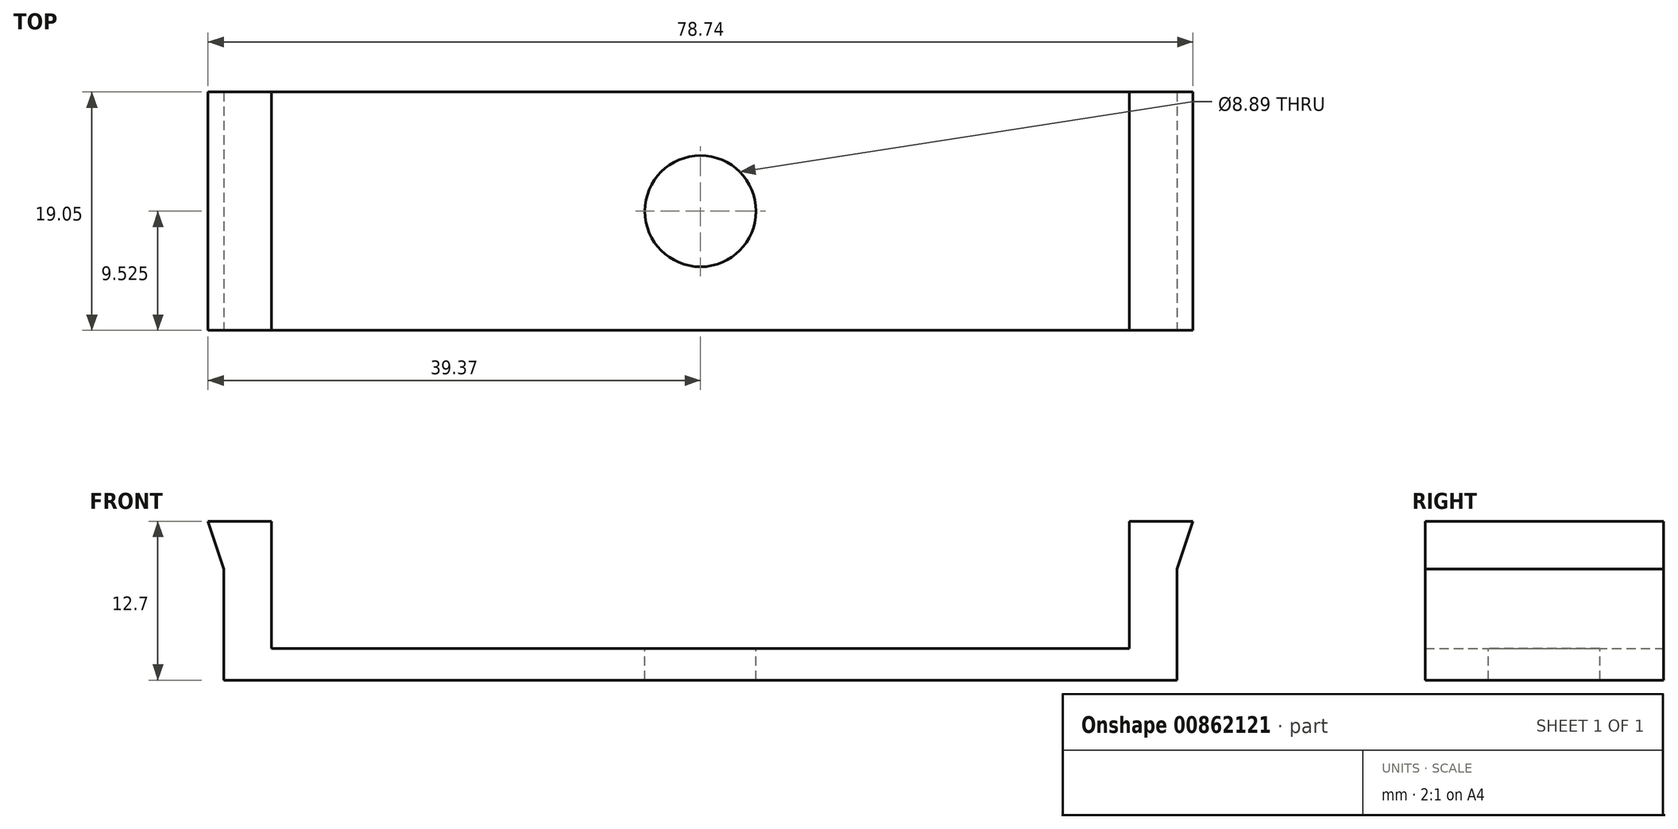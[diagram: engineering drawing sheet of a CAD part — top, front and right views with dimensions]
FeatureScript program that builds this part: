
annotation { "Feature Type Name" : "Feature", "Feature Type Description" : "" }
export const myFeature = defineFeature(function(context is Context, id is Id, definition is map)
    precondition{}
    {
        {
            var Q0;
            Q0=qCreatedBy(makeId("Top.planeOp"),FACE);
            var sketch = newSketch(context, id + "F0", { "sketchPlane" : qUnion([Q0])});
            skLineSegment(sketch, "E0.bottom", {"start": v(0, 0) * mm, "end": v(76.2, 0) * mm});
            skLineSegment(sketch, "E0.top", {"start": v(0, 19.05) * mm, "end": v(76.2, 19.05) * mm});
            skLineSegment(sketch, "E0.left", {"start": v(0, 0) * mm, "end": v(0, 19.05) * mm});
            skLineSegment(sketch, "E0.right", {"start": v(76.2, 0) * mm, "end": v(76.2, 19.05) * mm});
            skSolve(sketch);
        }
        {
            var Q0;
            Q0=makeQuery(id+"F0.imprint","IMPRINT",FACE,{"disambiguationData":[TD([[makeQuery(id+"F0.imprint","IMPRINT",EDGE,{"derivedFrom":sQuery(id+"F0.wireOp",EDGE,"E0.bottom")}),1.0]])]});
            extrude(context, id + "F1", {"entities" : qUnion([Q0]), "depth" : 2.54 * mm, "offsetDistance" : 25.4 * mm});
        }
        {
            var Q0;
            Q0=makeQuery(id+"F1.opExtrude","CAP_FACE",FACE,{"disambiguationData":[OSD([sQuery(id+"F0.wireOp",EDGE,"E0.bottom"),sQuery(id+"F0.wireOp",EDGE,"E0.top"),sQuery(id+"F0.wireOp",EDGE,"E0.left"),sQuery(id+"F0.wireOp",EDGE,"E0.right")])],"isStart":false});
            var sketch = newSketch(context, id + "F2", { "sketchPlane" : qUnion([Q0])});
            skLineSegment(sketch, "E1.bottom", {"start": v(76.2, 19.05) * mm, "end": v(72.4, 19.05) * mm});
            skLineSegment(sketch, "E1.top", {"start": v(76.2, 0) * mm, "end": v(72.4, 0) * mm});
            skLineSegment(sketch, "E1.left", {"start": v(76.2, 19.05) * mm, "end": v(76.2, 0) * mm});
            skLineSegment(sketch, "E1.right", {"start": v(72.4, 19.05) * mm, "end": v(72.4, 0) * mm});
            skLineSegment(sketch, "E2.bottom", {"start": v(0, 0) * mm, "end": v(3.8, 0) * mm});
            skLineSegment(sketch, "E2.top", {"start": v(0, 19.05) * mm, "end": v(3.8, 19.05) * mm});
            skLineSegment(sketch, "E2.left", {"start": v(0, 0) * mm, "end": v(0, 19.05) * mm});
            skLineSegment(sketch, "E2.right", {"start": v(3.8, 0) * mm, "end": v(3.8, 19.05) * mm});
            skSolve(sketch);
        }
        {
            var Q0;
            Q0=makeQuery(id+"F2.imprint","IMPRINT",FACE,{"disambiguationData":[TD([[makeQuery(id+"F2.imprint","IMPRINT",EDGE,{"derivedFrom":sQuery(id+"F2.wireOp",EDGE,"E2.bottom")}),1.0]])]});
            var Q1;
            Q1=makeQuery(id+"F2.imprint","IMPRINT",FACE,{"disambiguationData":[TD([[makeQuery(id+"F2.imprint","IMPRINT",EDGE,{"derivedFrom":sQuery(id+"F2.wireOp",EDGE,"E1.bottom")}),-1.0]])]});
            extrude(context, id + "F3", {"entities" : qUnion([Q0, Q1]), "operationType" : NewBodyOperationType.ADD, "depth" : 10.16 * mm, "offsetDistance" : 25.4 * mm});
        }
        {
            var Q0;
            Q0=makeQuery(id+"F1.opExtrude","CAP_FACE",FACE,{"disambiguationData":[OSD([sQuery(id+"F0.wireOp",EDGE,"E0.bottom"),sQuery(id+"F0.wireOp",EDGE,"E0.top"),sQuery(id+"F0.wireOp",EDGE,"E0.left"),sQuery(id+"F0.wireOp",EDGE,"E0.right")])],"isStart":false});
            var sketch = newSketch(context, id + "F4", { "sketchPlane" : qUnion([Q0])});
            skLineSegment(sketch, "E3", {"start": v(3.81, 9.52) * mm, "end": v(72.4, 9.52) * mm, "construction": true});
            skCircle(sketch, "E4", {"center": v(38.1, 9.52) * mm, "radius": 4.45 * mm});
            skSolve(sketch);
        }
        {
            var Q0;
            Q0=makeQuery(id+"F4.imprint","IMPRINT",FACE,{"disambiguationData":[TD([[makeQuery(id+"F4.imprint","IMPRINT",EDGE,{"derivedFrom":sQuery(id+"F4.wireOp",EDGE,"E4")}),1.0]])]});
            extrude(context, id + "F5", {"entities" : qUnion([Q0]), "operationType" : NewBodyOperationType.REMOVE, "oppositeDirection" : true, "depth" : 25.4 * mm, "offsetDistance" : 25.4 * mm});
        }
        {
            var Q0;
            Q0=makeQuery(id+"F3.boolean.opBoolean","MERGE",FACE,{"derivedFrom":[makeQuery(id+"F1.opExtrude","SWEPT_FACE",FACE,{"disambiguationData":[OSD([sQuery(id+"F0.wireOp",EDGE,"E0.bottom")])]}),makeQuery(id+"F3.opExtrude","SWEPT_FACE",FACE,{"disambiguationData":[OSD([sQuery(id+"F2.wireOp",EDGE,"E1.top")])]}),makeQuery(id+"F3.opExtrude","SWEPT_FACE",FACE,{"disambiguationData":[OSD([sQuery(id+"F2.wireOp",EDGE,"E2.bottom")])]})]});
            var sketch = newSketch(context, id + "F6", { "sketchPlane" : qUnion([Q0])});
            skLineSegment(sketch, "E5", {"start": v(0, 12.7) * mm, "end": v(-1.27, 12.7) * mm});
            skLineSegment(sketch, "E6", {"start": v(-1.27, 12.7) * mm, "end": v(0, 8.9) * mm});
            skLineSegment(sketch, "E7", {"start": v(0, 12.7) * mm, "end": v(0, 8.9) * mm});
            skLineSegment(sketch, "E8", {"start": v(76.2, 12.7) * mm, "end": v(77.47, 12.7) * mm});
            skLineSegment(sketch, "E9", {"start": v(77.47, 12.7) * mm, "end": v(76.2, 8.9) * mm});
            skLineSegment(sketch, "E10", {"start": v(76.2, 12.7) * mm, "end": v(76.2, 8.9) * mm});
            skSolve(sketch);
        }
        {
            var Q0;
            Q0=makeQuery(id+"F6.imprint","IMPRINT",FACE,{"disambiguationData":[TD([[makeQuery(id+"F6.imprint","IMPRINT",EDGE,{"derivedFrom":sQuery(id+"F6.wireOp",EDGE,"E5")}),1.0]])]});
            var Q1;
            Q1=makeQuery(id+"F6.imprint","IMPRINT",FACE,{"disambiguationData":[TD([[makeQuery(id+"F6.imprint","IMPRINT",EDGE,{"derivedFrom":sQuery(id+"F6.wireOp",EDGE,"E8")}),-1.0]])]});
            var Q2;
            Q2=makeQuery(id+"F3.boolean.opBoolean","MERGE",FACE,{"derivedFrom":[makeQuery(id+"F1.opExtrude","SWEPT_FACE",FACE,{"disambiguationData":[OSD([sQuery(id+"F0.wireOp",EDGE,"E0.top")])]}),makeQuery(id+"F3.opExtrude","SWEPT_FACE",FACE,{"disambiguationData":[OSD([sQuery(id+"F2.wireOp",EDGE,"E1.bottom")])]}),makeQuery(id+"F3.opExtrude","SWEPT_FACE",FACE,{"disambiguationData":[OSD([sQuery(id+"F2.wireOp",EDGE,"E2.top")])]})]});
            extrude(context, id + "F7", {"entities" : qUnion([Q0, Q1]), "operationType" : NewBodyOperationType.ADD, "endBound" : BoundingType.UP_TO_SURFACE, "oppositeDirection" : true, "depth" : 25.4 * mm, "endBoundEntityFace" : qUnion([Q2]), "offsetDistance" : 25.4 * mm});
        }
    });
